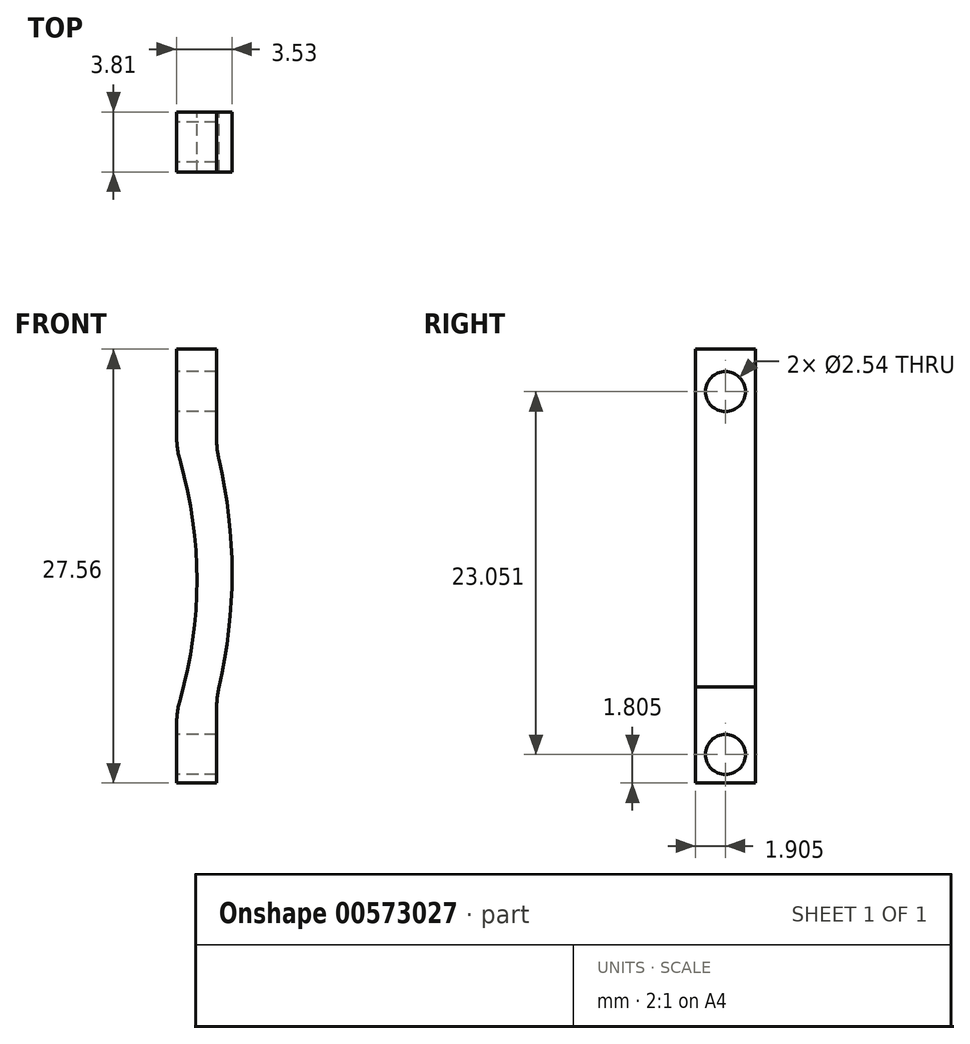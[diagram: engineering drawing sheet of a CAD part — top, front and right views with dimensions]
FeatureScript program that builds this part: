
annotation { "Feature Type Name" : "Feature", "Feature Type Description" : "" }
export const myFeature = defineFeature(function(context is Context, id is Id, definition is map)
    precondition{}
    {
        {
            var Q0;
            Q0=qCreatedBy(makeId("Front.planeOp"),FACE);
            var sketch = newSketch(context, id + "F0", { "sketchPlane" : qUnion([Q0])});
            skLineSegment(sketch, "E0", {"start": v(0, 0) * mm, "end": v(0, 2.62) * mm});
            skLineSegment(sketch, "E1", {"start": v(0, 0) * mm, "end": v(2.54, 0) * mm});
            skPoint(sketch, "E2.visualSharp", {"position": v(2.54, 5.08) * mm});
            skPoint(sketch, "E3.visualSharp", {"position": v(0, 5.08) * mm});
            skLineSegment(sketch, "E3.filletArc", {"start": v(0, 3.56) * mm, "end": v(0, 3.56) * mm});
            skArc(sketch, "E4", {"start": v(0.25, 4.37) * mm, "mid": v(1.3, 11.89) * mm, "end": v(0.25, 19.41) * mm});
            skLineSegment(sketch, "E5", {"start": v(0, 21.16) * mm, "end": v(0, 26.57) * mm});
            skLineSegment(sketch, "E6", {"start": v(0, 26.57) * mm, "end": v(2.54, 26.57) * mm});
            skLineSegment(sketch, "E7", {"start": v(2.54, 26.57) * mm, "end": v(2.54, 20.98) * mm});
            skArc(sketch, "E8", {"start": v(2.7, 5.11) * mm, "mid": v(3.53, 12.33) * mm, "end": v(2.7, 19.55) * mm});
            skPoint(sketch, "E9.visualSharp", {"position": v(0, 20.22) * mm});
            skArc(sketch, "E9.filletArc", {"start": v(0, 21.16) * mm, "mid": v(0.06, 20.28) * mm, "end": v(0.25, 19.41) * mm});
            skPoint(sketch, "E10.visualSharp", {"position": v(2.54, 20.22) * mm});
            skArc(sketch, "E10.filletArc", {"start": v(2.54, 20.98) * mm, "mid": v(2.58, 20.26) * mm, "end": v(2.7, 19.55) * mm});
            skPoint(sketch, "E11.visualSharp", {"position": v(2.54, 4.44) * mm});
            skPoint(sketch, "E12.visualSharp", {"position": v(0, 3.56) * mm});
            skLineSegment(sketch, "E13", {"start": v(2.54, 0) * mm, "end": v(2.54, 3.56) * mm});
            skArc(sketch, "E14", {"start": v(2.7, 5.11) * mm, "mid": v(2.58, 4.34) * mm, "end": v(2.54, 3.56) * mm});
            skArc(sketch, "E15", {"start": v(0.25, 4.37) * mm, "mid": v(0.06, 3.5) * mm, "end": v(0, 2.62) * mm});
            skSolve(sketch);
        }
        {
            var Q0;
            Q0 = qSketchRegion(id + "F0", true);
            extrude(context, id + "F1", {"entities" : qUnion([Q0]), "depth" : 3.8 * mm, "offsetDistance" : 25.4 * mm});
        }
        {
            var Q0;
            Q0=makeQuery(id+"F1.opExtrude","SWEPT_FACE",FACE,{"disambiguationData":[OSD([sQuery(id+"F0.wireOp",EDGE,"E5")])]});
            var sketch = newSketch(context, id + "F2", { "sketchPlane" : qUnion([Q0])});
            skCircle(sketch, "E16", {"center": v(1.9, 23.87) * mm, "radius": 1.27 * mm});
            skPoint(sketch, "E17.orphan", {"position": v(1.9, 26.57) * mm});
            skPoint(sketch, "E18.end.orphan", {"position": v(1.9, 21.16) * mm});
            skSolve(sketch);
        }
        {
            var Q0;
            Q0 = qSketchRegion(id + "F2", true);
            extrude(context, id + "F3", {"entities" : qUnion([Q0]), "operationType" : NewBodyOperationType.REMOVE, "oppositeDirection" : true, "depth" : 10.67 * mm, "offsetDistance" : 25.4 * mm});
        }
        {
            var Q0;
            Q0=makeQuery(id+"F1.opExtrude","SWEPT_FACE",FACE,{"disambiguationData":[OSD([sQuery(id+"F0.wireOp",EDGE,"E1")])]});
            var sketch = newSketch(context, id + "F4", { "sketchPlane" : qUnion([Q0])});
            skLineSegment(sketch, "E19.0.0", {"start": v(0, 0) * mm, "end": v(2.54, 0) * mm});
            skLineSegment(sketch, "E19.0.1", {"start": v(2.54, 0) * mm, "end": v(2.54, 3.81) * mm});
            skLineSegment(sketch, "E19.0.2", {"start": v(2.54, 3.81) * mm, "end": v(0, 3.81) * mm});
            skLineSegment(sketch, "E19.0.3", {"start": v(0, 3.81) * mm, "end": v(0, 0) * mm});
            skSolve(sketch);
        }
        {
            var Q0;
            Q0 = qSketchRegion(id + "F4", true);
            extrude(context, id + "F5", {"entities" : qUnion([Q0]), "operationType" : NewBodyOperationType.ADD, "depth" : 1 * mm, "offsetDistance" : 25.4 * mm});
        }
        {
            var Q0;
            Q0=makeQuery(id+"F5.boolean.opBoolean","MERGE",FACE,{"derivedFrom":[makeQuery(id+"F1.opExtrude","SWEPT_FACE",FACE,{"disambiguationData":[OSD([sQuery(id+"F0.wireOp",EDGE,"E0")])]}),makeQuery(id+"F5.opExtrude","SWEPT_FACE",FACE,{"disambiguationData":[OSD([sQuery(id+"F4.wireOp",EDGE,"E19.0.3")])]})]});
            var sketch = newSketch(context, id + "F6", { "sketchPlane" : qUnion([Q0])});
            skLineSegment(sketch, "E20", {"start": v(1.9, 2.62) * mm, "end": v(1.9, -1) * mm});
            skCircle(sketch, "E21", {"center": v(1.9, 0.81) * mm, "radius": 1.27 * mm});
            skSolve(sketch);
        }
        {
            var Q0;
            Q0 = qSketchRegion(id + "F6", true);
            extrude(context, id + "F7", {"entities" : qUnion([Q0]), "operationType" : NewBodyOperationType.REMOVE, "oppositeDirection" : true, "depth" : 25.4 * mm, "offsetDistance" : 25.4 * mm});
        }
    });
